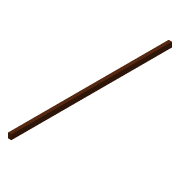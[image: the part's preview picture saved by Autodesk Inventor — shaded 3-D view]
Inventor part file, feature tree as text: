
AUTODESK INVENTOR PART (.ipt)
format: ipt  version: 2016 SP2 (Build 200236200, 236)  size: 101,376 bytes
history: native  units: in
note: dims shown in document units (in); Inventor stores cm internally (conversion verified against a paired STEP export)
features: extrude x2, sketch x2
ambient origin geometry x8: Origin, YZ Plane, XZ Plane, XY Plane, X Axis, Y Axis, Z Axis, Center Point
bodies: Solid1 (feature_tree)
feature tree (4):
  extrude  "Extrusion1"  Depth=4.4882in
  extrude  "Extrusion4"  Depth=10.0in
  sketch  "Sketch1"  dims[d0=2.9528in d1=4.4882in]
  sketch  "Sketch4"  dims[d2=144.0in d3=0.0in d16=1.0in d18=10.0in d19=0.0in]
